# Revit family: Door-Automatic_Fire_Vent-Bilco-Double_Leaf
name_source: partatom
category: Doors
revit_build: Autodesk Revit 2018 (Build: 20181011_1500(x64)
units: mm (PartAtom-declared; Revit-internal decimal feet)

## family parameters
Cut with Voids When Loaded = No
Host = Face
OmniClass Number = 23.30.10.27.24
OmniClass Title = Roof Hatches
Room Calculation Point = No
Shared = No

## types (1)
- Door-Automatic_Fire_Vent-Bilco-Double_Leaf
    Analytic Construction = <None>
    Center Beam Width = 6 1/2"
    Cover Length = 94"
    Cover Material = Galvanized Steel-Bilco-Red Oxide Primer Finish
    Cover Opening = 90.00°
    Cover Panel Material = Plastic-Bilco-Polycarbonate-Translucent
    Cover Type = Cover-Bilco-STC_50-OITC_46_Sound_Rating : By Type
    Cover Width = 52 1/4"
    DD Width = 24"
    Default Elevation = 48"
    Description = Automatic Fire Vent
    Fiberboard Insulation Material = Insulation-Bilco-Rigid Insulation
    Frame Material = Stainless Steel-Bilco-Sand Blast Finish-304
    Frame Type = Frame-Bilco-STC_50-OITC_46_Sound_Rating : By Type
    Hardware Material = Stainless Steel-Bilco-Sand Blast Finish-304
    Height = 12 19/32"
    Length = 90"
    Lifting Height = 7 1/4"
    Lifting Mechanism = Lifting_Mechanism-Bilco-Shock_Absorber
    Lifting Width = 6 5/8"
    Manufacturer = Bilco
    Model = ACDSH4890
    Product Documentation Link = http://www.bilco.com
    Product Page URL = https://www.bilco.com
    Release System Handle Offset = 4"
    Release System Offset = 1/4"
    Rough Height = 90"
    Rough Width = 48"
    URL = http://www.bilco.com
    Width = 48"
    With Arm Guide = No
    With Sound Rating = Yes
    Without Arm Guide = Yes
    Without Sound Rating = No

## geometry (parser evidence)
native form markers: Sweep x37
no freeform markers — native parametric forms only
